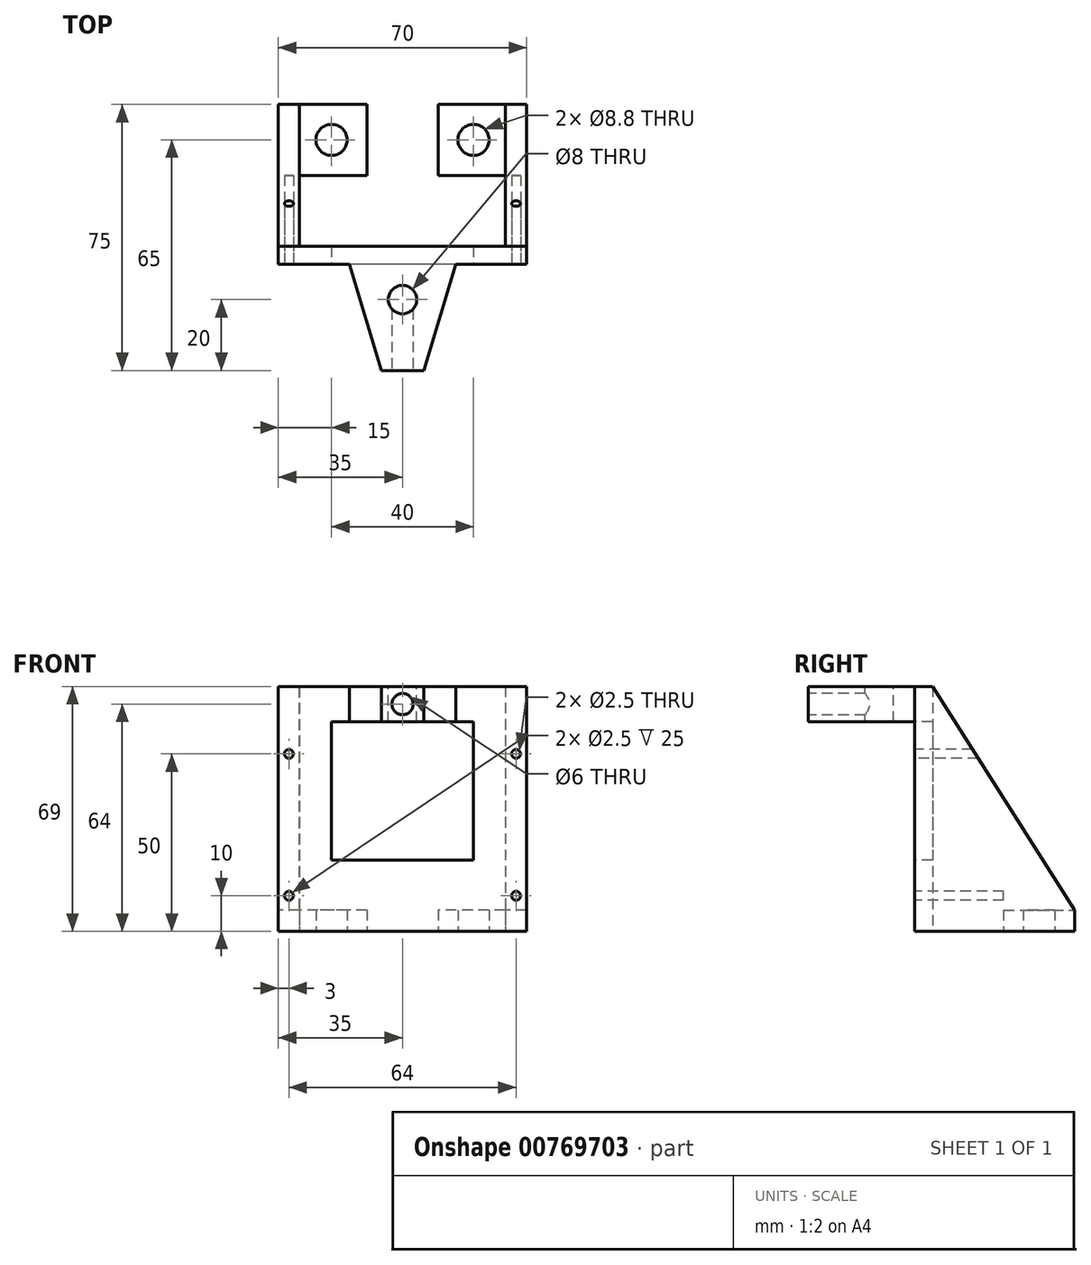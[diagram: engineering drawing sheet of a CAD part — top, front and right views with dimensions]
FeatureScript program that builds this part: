
annotation { "Feature Type Name" : "Feature", "Feature Type Description" : "" }
export const myFeature = defineFeature(function(context is Context, id is Id, definition is map)
    precondition{}
    {
        {
            var Q0;
            Q0=qCreatedBy(makeId("Top.planeOp"),FACE);
            var sketch = newSketch(context, id + "F0", { "sketchPlane" : qUnion([Q0])});
            skLineSegment(sketch, "E0.bottom", {"start": v(35, -37.5) * mm, "end": v(-35, -37.5) * mm});
            skLineSegment(sketch, "E0.top", {"start": v(35, 37.5) * mm, "end": v(-35, 37.5) * mm});
            skLineSegment(sketch, "E0.left", {"start": v(35, -37.5) * mm, "end": v(35, 37.5) * mm});
            skLineSegment(sketch, "E0.right", {"start": v(-35, -37.5) * mm, "end": v(-35, 37.5) * mm});
            skPoint(sketch, "E0.middle", {"position": v(0, 0) * mm});
            skLineSegment(sketch, "E1", {"start": v(-35, 37.5) * mm, "end": v(-10, 37.5) * mm, "construction": true});
            skLineSegment(sketch, "E2.MirrorCS", {"start": v(35, 37.5) * mm, "end": v(10, 37.5) * mm, "construction": true});
            skLineSegment(sketch, "E3", {"start": v(-10, 37.5) * mm, "end": v(-10, 17.5) * mm, "construction": true});
            skLineSegment(sketch, "E4.MirrorCS", {"start": v(10, 37.5) * mm, "end": v(10, 17.5) * mm, "construction": true});
            skLineSegment(sketch, "E5", {"start": v(-35, 37.5) * mm, "end": v(-35, 27.5) * mm, "construction": true});
            skLineSegment(sketch, "E6", {"start": v(-35, 27.5) * mm, "end": v(-20, 27.5) * mm, "construction": true});
            skLineSegment(sketch, "E7.MirrorCS", {"start": v(35, 27.5) * mm, "end": v(20, 27.5) * mm, "construction": true});
            skCircle(sketch, "E8", {"center": v(-20, 27.5) * mm, "radius": 4.4 * mm});
            skCircle(sketch, "E9.MirrorC", {"center": v(20, 27.5) * mm, "radius": 4.4 * mm});
            skLineSegment(sketch, "E10", {"start": v(-35, 27.5) * mm, "end": v(-35, -2.5) * mm, "construction": true});
            skLineSegment(sketch, "E11", {"start": v(-35, -37.5) * mm, "end": v(-29, -37.5) * mm, "construction": true});
            skLineSegment(sketch, "E12", {"start": v(-10, 17.5) * mm, "end": v(-35, 17.5) * mm, "construction": true});
            skLineSegment(sketch, "E13", {"start": v(-29, -37.5) * mm, "end": v(-29, 17.5) * mm, "construction": true});
            skLineSegment(sketch, "E14.MirrorCS", {"start": v(10, 17.5) * mm, "end": v(35, 17.5) * mm, "construction": true});
            skLineSegment(sketch, "E15.MirrorCS", {"start": v(29, -37.5) * mm, "end": v(29, 17.5) * mm, "construction": true});
            skLineSegment(sketch, "E16", {"start": v(-35, -2.5) * mm, "end": v(35, -2.5) * mm, "construction": true});
            skLineSegment(sketch, "E17", {"start": v(-10, 37.5) * mm, "end": v(-10, 17.5) * mm});
            skLineSegment(sketch, "E18", {"start": v(-29, 17.5) * mm, "end": v(-29, -2.5) * mm});
            skLineSegment(sketch, "E19", {"start": v(-29, -2.5) * mm, "end": v(29, -2.5) * mm});
            skLineSegment(sketch, "E20", {"start": v(29, -2.5) * mm, "end": v(29, 17.5) * mm});
            skLineSegment(sketch, "E21", {"start": v(10, 17.5) * mm, "end": v(10, 37.5) * mm});
            skLineSegment(sketch, "E22", {"start": v(10, 17.5) * mm, "end": v(29, 17.5) * mm});
            skLineSegment(sketch, "E23", {"start": v(-29, 17.5) * mm, "end": v(-10, 17.5) * mm});
            skSolve(sketch);
        }
        {
            var Q0;
            Q0=makeQuery(id+"F0.imprint","IMPRINT",FACE,{"disambiguationData":[TD([[makeQuery(id+"F0.imprint","IMPRINT",EDGE,{"derivedFrom":sQuery(id+"F0.wireOp",EDGE,"E0.bottom")}),-1.0]])]});
            extrude(context, id + "F1", {"entities" : qUnion([Q0]), "depth" : 69 * mm, "offsetDistance" : 25 * mm});
        }
        {
            var Q0;
            Q0=makeQuery(id+"F1.opExtrude","SWEPT_FACE",FACE,{"disambiguationData":[OSD([sQuery(id+"F0.wireOp",EDGE,"E0.right")])]});
            var sketch = newSketch(context, id + "F2", { "sketchPlane" : qUnion([Q0])});
            skLineSegment(sketch, "E24.bottom", {"start": v(37.5, 69) * mm, "end": v(7.5, 69) * mm, "construction": true});
            skLineSegment(sketch, "E24.top", {"start": v(37.5, 59) * mm, "end": v(7.5, 59) * mm, "construction": true});
            skLineSegment(sketch, "E24.left", {"start": v(37.5, 69) * mm, "end": v(37.5, 59) * mm, "construction": true});
            skLineSegment(sketch, "E24.right", {"start": v(7.5, 69) * mm, "end": v(7.5, 59) * mm, "construction": true});
            skLineSegment(sketch, "E25.bottom", {"start": v(7.5, 59) * mm, "end": v(37.5, 59) * mm});
            skLineSegment(sketch, "E25.top", {"start": v(7.5, 0) * mm, "end": v(37.5, 0) * mm});
            skLineSegment(sketch, "E25.left", {"start": v(7.5, 59) * mm, "end": v(7.5, 0) * mm});
            skLineSegment(sketch, "E25.right", {"start": v(37.5, 59) * mm, "end": v(37.5, 0) * mm});
            skLineSegment(sketch, "E26.bottom", {"start": v(-37.5, 0) * mm, "end": v(2.5, 0) * mm, "construction": true});
            skLineSegment(sketch, "E26.top", {"start": v(-37.5, 6) * mm, "end": v(2.5, 6) * mm, "construction": true});
            skLineSegment(sketch, "E26.left", {"start": v(-37.5, 0) * mm, "end": v(-37.5, 6) * mm, "construction": true});
            skLineSegment(sketch, "E26.right", {"start": v(2.5, 0) * mm, "end": v(2.5, 6) * mm, "construction": true});
            skLineSegment(sketch, "E27.bottom", {"start": v(2.5, 6) * mm, "end": v(-37.5, 6) * mm});
            skLineSegment(sketch, "E27.top", {"start": v(2.5, 69) * mm, "end": v(-37.5, 69) * mm});
            skLineSegment(sketch, "E27.left", {"start": v(2.5, 6) * mm, "end": v(2.5, 69) * mm});
            skLineSegment(sketch, "E27.right", {"start": v(-37.5, 6) * mm, "end": v(-37.5, 69) * mm});
            skSolve(sketch);
        }
        {
            var Q0;
            Q0=makeQuery(id+"F2.imprint","IMPRINT",FACE,{"disambiguationData":[TD([[makeQuery(id+"F2.imprint","IMPRINT",EDGE,{"derivedFrom":sQuery(id+"F2.wireOp",EDGE,"E25.bottom")}),-1.0]])]});
            extrude(context, id + "F3", {"entities" : qUnion([Q0]), "operationType" : NewBodyOperationType.REMOVE, "endBound" : BoundingType.THROUGH_ALL, "oppositeDirection" : true, "depth" : 25 * mm, "offsetDistance" : 25 * mm});
        }
        {
            var Q0;
            Q0=makeQuery(id+"F1.opExtrude","CAP_FACE",FACE,{"disambiguationData":[OSD([sQuery(id+"F0.wireOp",EDGE,"E0.bottom"),sQuery(id+"F0.wireOp",EDGE,"E0.top"),sQuery(id+"F0.wireOp",EDGE,"E0.left"),sQuery(id+"F0.wireOp",EDGE,"E0.right"),sQuery(id+"F0.wireOp",EDGE,"E8"),sQuery(id+"F0.wireOp",EDGE,"E9.MirrorC"),sQuery(id+"F0.wireOp",EDGE,"E17"),sQuery(id+"F0.wireOp",EDGE,"E18"),sQuery(id+"F0.wireOp",EDGE,"E19"),sQuery(id+"F0.wireOp",EDGE,"E20"),sQuery(id+"F0.wireOp",EDGE,"E21"),sQuery(id+"F0.wireOp",EDGE,"E22"),sQuery(id+"F0.wireOp",EDGE,"E23")])],"isStart":false});
            var sketch = newSketch(context, id + "F4", { "sketchPlane" : qUnion([Q0])});
            skLineSegment(sketch, "E28.bottom", {"start": v(29, 17.5) * mm, "end": v(-29, 17.5) * mm});
            skLineSegment(sketch, "E28.top", {"start": v(29, 37.5) * mm, "end": v(-29, 37.5) * mm});
            skLineSegment(sketch, "E28.left", {"start": v(29, 17.5) * mm, "end": v(29, 37.5) * mm});
            skLineSegment(sketch, "E28.right", {"start": v(-29, 17.5) * mm, "end": v(-29, 37.5) * mm});
            skSolve(sketch);
        }
        {
            var Q0;
            {var subQ3=sQuery(id+"F4.wireOp",EDGE,"E28.left");Q0=makeQuery(id+"F4.imprint","IMPRINT",FACE,{"disambiguationData":[TD([[makeQuery(id+"F4.imprint","IMPRINT",EDGE,{"derivedFrom":subQ3}),1.0]])]});}
            var Q1;
            {var subQ0=sQuery(id+"F4.wireOp",EDGE,"E28.right");Q1=makeQuery(id+"F4.imprint","IMPRINT",FACE,{"disambiguationData":[TD([[makeQuery(id+"F4.imprint","IMPRINT",EDGE,{"derivedFrom":subQ0}),-1.0]])]});}
            extrude(context, id + "F5", {"entities" : qUnion([Q0, Q1]), "operationType" : NewBodyOperationType.REMOVE, "oppositeDirection" : true, "depth" : 63 * mm, "offsetDistance" : 25 * mm});
        }
        {
            var Q0;
            Q0=makeQuery(id+"F1.opExtrude","SWEPT_FACE",FACE,{"disambiguationData":[OSD([sQuery(id+"F0.wireOp",EDGE,"E0.right")])]});
            var sketch = newSketch(context, id + "F6", { "sketchPlane" : qUnion([Q0])});
            skLineSegment(sketch, "E29.bottom", {"start": v(-37.5, 69) * mm, "end": v(2.5, 69) * mm, "construction": true});
            skLineSegment(sketch, "E29.top", {"start": v(-37.5, 6) * mm, "end": v(2.5, 6) * mm, "construction": true});
            skLineSegment(sketch, "E29.left", {"start": v(-37.5, 69) * mm, "end": v(-37.5, 6) * mm, "construction": true});
            skLineSegment(sketch, "E29.right", {"start": v(2.5, 69) * mm, "end": v(2.5, 6) * mm, "construction": true});
            skLineSegment(sketch, "E30", {"start": v(-37.5, 69) * mm, "end": v(2.5, 69) * mm});
            skLineSegment(sketch, "E31", {"start": v(2.5, 69) * mm, "end": v(-37.5, 6) * mm});
            skLineSegment(sketch, "E32", {"start": v(-37.5, 6) * mm, "end": v(-37.5, 69) * mm});
            skSolve(sketch);
        }
        {
            var Q0;
            Q0=makeQuery(id+"F6.imprint","IMPRINT",FACE,{"disambiguationData":[TD([[makeQuery(id+"F6.imprint","IMPRINT",EDGE,{"derivedFrom":sQuery(id+"F6.wireOp",EDGE,"E30")}),1.0]])]});
            extrude(context, id + "F7", {"entities" : qUnion([Q0]), "operationType" : NewBodyOperationType.REMOVE, "endBound" : BoundingType.THROUGH_ALL, "oppositeDirection" : true, "depth" : 25 * mm, "offsetDistance" : 25 * mm});
        }
        {
            var Q0;
            Q0=makeQuery(id+"F3.boolean.opBoolean","COPY",FACE,{"derivedFrom":makeQuery(id+"F3.opExtrude","SWEPT_FACE",FACE,{"disambiguationData":[OSD([sQuery(id+"F2.wireOp",EDGE,"E25.left")])]})});
            var sketch = newSketch(context, id + "F8", { "sketchPlane" : qUnion([Q0])});
            skLineSegment(sketch, "E33", {"start": v(35, 0) * mm, "end": v(35, 20) * mm, "construction": true});
            skLineSegment(sketch, "E34", {"start": v(35, 20) * mm, "end": v(20, 20) * mm, "construction": true});
            skLineSegment(sketch, "E35.bottom", {"start": v(20, 20) * mm, "end": v(-20, 20) * mm});
            skLineSegment(sketch, "E35.top", {"start": v(20, 59) * mm, "end": v(-20, 59) * mm});
            skLineSegment(sketch, "E35.left", {"start": v(20, 20) * mm, "end": v(20, 59) * mm});
            skLineSegment(sketch, "E35.right", {"start": v(-20, 20) * mm, "end": v(-20, 59) * mm});
            skSolve(sketch);
        }
        {
            var Q0;
            Q0=makeQuery(id+"F8.imprint","IMPRINT",FACE,{"disambiguationData":[TD([[makeQuery(id+"F8.imprint","IMPRINT",EDGE,{"derivedFrom":sQuery(id+"F8.wireOp",EDGE,"E35.bottom")}),-1.0]])]});
            extrude(context, id + "F9", {"entities" : qUnion([Q0]), "operationType" : NewBodyOperationType.REMOVE, "endBound" : BoundingType.THROUGH_ALL, "oppositeDirection" : true, "depth" : 25 * mm, "offsetDistance" : 25 * mm});
        }
        {
            var Q0;
            Q0=makeQuery(id+"F1.opExtrude","CAP_FACE",FACE,{"disambiguationData":[OSD([sQuery(id+"F0.wireOp",EDGE,"E0.bottom"),sQuery(id+"F0.wireOp",EDGE,"E0.top"),sQuery(id+"F0.wireOp",EDGE,"E0.left"),sQuery(id+"F0.wireOp",EDGE,"E0.right"),sQuery(id+"F0.wireOp",EDGE,"E8"),sQuery(id+"F0.wireOp",EDGE,"E9.MirrorC"),sQuery(id+"F0.wireOp",EDGE,"E17"),sQuery(id+"F0.wireOp",EDGE,"E18"),sQuery(id+"F0.wireOp",EDGE,"E19"),sQuery(id+"F0.wireOp",EDGE,"E20"),sQuery(id+"F0.wireOp",EDGE,"E21"),sQuery(id+"F0.wireOp",EDGE,"E22"),sQuery(id+"F0.wireOp",EDGE,"E23")])],"isStart":false});
            var sketch = newSketch(context, id + "F10", { "sketchPlane" : qUnion([Q0])});
            skLineSegment(sketch, "E36", {"start": v(-35, -37.5) * mm, "end": v(-35, -17.5) * mm, "construction": true});
            skLineSegment(sketch, "E37", {"start": v(-35, -17.5) * mm, "end": v(35, -17.5) * mm, "construction": true});
            skCircle(sketch, "E38", {"center": v(0, -17.5) * mm, "radius": 4 * mm});
            skPoint(sketch, "E38.centerSnap0", {"position": v(0, -17.5) * mm});
            skSolve(sketch);
        }
        {
            var Q0;
            Q0=makeQuery(id+"F10.imprint","IMPRINT",FACE,{"disambiguationData":[TD([[makeQuery(id+"F10.imprint","IMPRINT",EDGE,{"derivedFrom":sQuery(id+"F10.wireOp",EDGE,"E38")}),1.0]])]});
            extrude(context, id + "F11", {"entities" : qUnion([Q0]), "operationType" : NewBodyOperationType.REMOVE, "endBound" : BoundingType.THROUGH_ALL, "oppositeDirection" : true, "depth" : 25 * mm, "offsetDistance" : 25 * mm});
        }
        {
            var Q0;
            Q0=makeQuery(id+"F1.opExtrude","SWEPT_FACE",FACE,{"disambiguationData":[OSD([sQuery(id+"F0.wireOp",EDGE,"E0.bottom")])]});
            var sketch = newSketch(context, id + "F12", { "sketchPlane" : qUnion([Q0])});
            skLineSegment(sketch, "E39", {"start": v(0, 69) * mm, "end": v(0, 64) * mm, "construction": true});
            skCircle(sketch, "E40", {"center": v(0, 64) * mm, "radius": 3 * mm});
            skSolve(sketch);
        }
        {
            var Q0;
            Q0=makeQuery(id+"F12.imprint","IMPRINT",FACE,{"disambiguationData":[TD([[makeQuery(id+"F12.imprint","IMPRINT",EDGE,{"derivedFrom":sQuery(id+"F12.wireOp",EDGE,"E40")}),1.0]])]});
            extrude(context, id + "F13", {"entities" : qUnion([Q0]), "operationType" : NewBodyOperationType.REMOVE, "endBound" : BoundingType.UP_TO_NEXT, "oppositeDirection" : true, "depth" : 25 * mm, "offsetDistance" : 25 * mm});
        }
        {
            var Q0;
            Q0=makeQuery(id+"F1.opExtrude","CAP_FACE",FACE,{"disambiguationData":[OSD([sQuery(id+"F0.wireOp",EDGE,"E0.bottom"),sQuery(id+"F0.wireOp",EDGE,"E0.top"),sQuery(id+"F0.wireOp",EDGE,"E0.left"),sQuery(id+"F0.wireOp",EDGE,"E0.right"),sQuery(id+"F0.wireOp",EDGE,"E8"),sQuery(id+"F0.wireOp",EDGE,"E9.MirrorC"),sQuery(id+"F0.wireOp",EDGE,"E17"),sQuery(id+"F0.wireOp",EDGE,"E18"),sQuery(id+"F0.wireOp",EDGE,"E19"),sQuery(id+"F0.wireOp",EDGE,"E20"),sQuery(id+"F0.wireOp",EDGE,"E21"),sQuery(id+"F0.wireOp",EDGE,"E22"),sQuery(id+"F0.wireOp",EDGE,"E23")])],"isStart":false});
            var sketch = newSketch(context, id + "F14", { "sketchPlane" : qUnion([Q0])});
            skLineSegment(sketch, "E41", {"start": v(-35, -2.5) * mm, "end": v(-35, -7.5) * mm, "construction": true});
            skLineSegment(sketch, "E42", {"start": v(0, -37.5) * mm, "end": v(-6, -37.5) * mm, "construction": true});
            skLineSegment(sketch, "E43.MirrorCS", {"start": v(0, -37.5) * mm, "end": v(6, -37.5) * mm, "construction": true});
            skLineSegment(sketch, "E44", {"start": v(0, -7.5) * mm, "end": v(-15, -7.5) * mm, "construction": true});
            skLineSegment(sketch, "E45.MirrorCS", {"start": v(0, -7.5) * mm, "end": v(15, -7.5) * mm, "construction": true});
            skLineSegment(sketch, "E46", {"start": v(-35, -7.5) * mm, "end": v(-15, -7.5) * mm});
            skLineSegment(sketch, "E47", {"start": v(-15, -7.5) * mm, "end": v(-6, -37.5) * mm});
            skLineSegment(sketch, "E48", {"start": v(-6, -37.5) * mm, "end": v(-35, -37.5) * mm});
            skLineSegment(sketch, "E49", {"start": v(-35, -7.5) * mm, "end": v(-35, -37.5) * mm});
            skLineSegment(sketch, "E50.MirrorCS", {"start": v(35, -7.5) * mm, "end": v(15, -7.5) * mm});
            skLineSegment(sketch, "E51.MirrorCS", {"start": v(35, -7.5) * mm, "end": v(35, -37.5) * mm});
            skLineSegment(sketch, "E52.MirrorCS", {"start": v(6, -37.5) * mm, "end": v(35, -37.5) * mm});
            skLineSegment(sketch, "E53.MirrorCS", {"start": v(15, -7.5) * mm, "end": v(6, -37.5) * mm});
            skSolve(sketch);
        }
        {
            var Q0;
            Q0=makeQuery(id+"F14.imprint","IMPRINT",FACE,{"disambiguationData":[TD([[makeQuery(id+"F14.imprint","IMPRINT",EDGE,{"derivedFrom":sQuery(id+"F14.wireOp",EDGE,"E47")}),-1.0]])]});
            var Q1;
            Q1=makeQuery(id+"F14.imprint","IMPRINT",FACE,{"disambiguationData":[TD([[makeQuery(id+"F14.imprint","IMPRINT",EDGE,{"derivedFrom":sQuery(id+"F14.wireOp",EDGE,"E50.MirrorCS")}),1.0]])]});
            extrude(context, id + "F15", {"entities" : qUnion([Q0, Q1]), "operationType" : NewBodyOperationType.REMOVE, "endBound" : BoundingType.THROUGH_ALL, "oppositeDirection" : true, "depth" : 25 * mm, "offsetDistance" : 25 * mm});
        }
        {
            var Q0;
            Q0=makeQuery(id+"F15.boolean.opBoolean","MERGE",FACE,{"derivedFrom":[makeQuery(id+"F3.boolean.opBoolean","COPY",FACE,{"derivedFrom":makeQuery(id+"F3.opExtrude","SWEPT_FACE",FACE,{"disambiguationData":[OSD([sQuery(id+"F2.wireOp",EDGE,"E25.left")])]})}),makeQuery(id+"F15.opExtrude","SWEPT_FACE",FACE,{"disambiguationData":[OSD([sQuery(id+"F14.wireOp",EDGE,"E46")])]}),makeQuery(id+"F15.opExtrude","SWEPT_FACE",FACE,{"disambiguationData":[OSD([sQuery(id+"F14.wireOp",EDGE,"E50.MirrorCS")])]})]});
            var sketch = newSketch(context, id + "F16", { "sketchPlane" : qUnion([Q0])});
            skLineSegment(sketch, "E54", {"start": v(-35, 0) * mm, "end": v(-32, 0) * mm, "construction": true});
            skLineSegment(sketch, "E55", {"start": v(-32, 0) * mm, "end": v(-32, 10) * mm, "construction": true});
            skLineSegment(sketch, "E56", {"start": v(-32, 10) * mm, "end": v(-32, 50) * mm, "construction": true});
            skCircle(sketch, "E57", {"center": v(-32, 50) * mm, "radius": 1.25 * mm});
            skCircle(sketch, "E58", {"center": v(-32, 10) * mm, "radius": 1.25 * mm});
            skLineSegment(sketch, "E59.MirrorCS", {"start": v(35, 0) * mm, "end": v(32, 0) * mm, "construction": true});
            skLineSegment(sketch, "E60.MirrorCS", {"start": v(32, 0) * mm, "end": v(32, 10) * mm, "construction": true});
            skLineSegment(sketch, "E61.MirrorCS", {"start": v(32, 10) * mm, "end": v(32, 50) * mm, "construction": true});
            skCircle(sketch, "E62.MirrorC", {"center": v(32, 50) * mm, "radius": 1.25 * mm});
            skCircle(sketch, "E63.MirrorC", {"center": v(32, 10) * mm, "radius": 1.25 * mm});
            skSolve(sketch);
        }
        {
            var Q0;
            Q0 = qSketchRegion(id + "F16", true);
            extrude(context, id + "F17", {"entities" : qUnion([Q0]), "operationType" : NewBodyOperationType.REMOVE, "oppositeDirection" : true, "depth" : 25 * mm, "offsetDistance" : 25 * mm});
        }
    });
